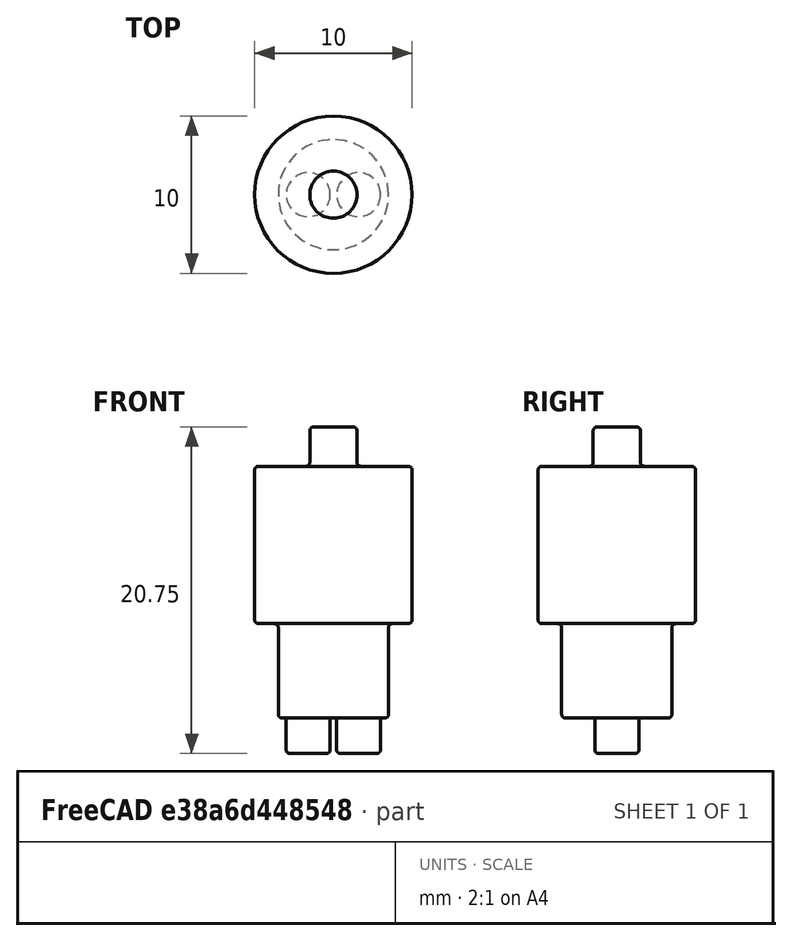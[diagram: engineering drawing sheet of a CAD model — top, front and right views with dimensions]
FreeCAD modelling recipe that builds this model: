
FCSTD DOCUMENT  (FreeCAD 1.0R38641 +468 (Git))
Label: optode
License: All rights reserved
LicenseURL: https://en.wikipedia.org/wiki/All_rights_reserved
objects: Part::Fillet×7, Part::Cylinder×5, Part::MultiFuse×1
note: 13 computed .brp shape members not serialized (recipe doc carries the construction recipe); baked Part::Feature solids carry a one-line shape summary decoded from their .brp

FEATURE [Part::Cylinder] cylinder
  Angle = 360
  AttacherType = Attacher::AttachEngine3D
  FirstAngle = 0
  Height = 10
  Radius = 5
  SecondAngle = 0
FEATURE [Part::Cylinder] cylinder001
  Angle = 360
  AttacherType = Attacher::AttachEngine3D
  FirstAngle = 0
  Height = 2.5
  Placement = pos=(0,0,10) rot=(0,0,1;0rad)
  Radius = 1.5
  SecondAngle = 0
FEATURE [Part::Cylinder] cylinder002
  Angle = 360
  AttacherType = Attacher::AttachEngine3D
  FirstAngle = 0
  Height = 6
  Placement = pos=(0,0,-6) rot=(0,0,1;0rad)
  Radius = 3.5
  SecondAngle = 0
FEATURE [Part::Cylinder] cylinder003
  Angle = 360
  AttacherType = Attacher::AttachEngine3D
  FirstAngle = 0
  Height = 8.25
  Placement = pos=(-1.6,0,-8.25) rot=(0,0,1;0rad)
  Radius = 1.4
  SecondAngle = 0
FEATURE [Part::Cylinder] cylinder004
  Angle = 360
  AttacherType = Attacher::AttachEngine3D
  FirstAngle = 0
  Height = 8.25
  Placement = pos=(1.6,0,-8.25) rot=(0,0,1;0rad)
  Radius = 1.4
  SecondAngle = 0
FEATURE [Part::MultiFuse] Group
  Refine = true
  Shapes = -> [cylinder,cylinder001,cylinder002,cylinder003,cylinder004]
FEATURE [Part::Fillet] Fillet
  Base = -> Group
  EdgeLinks = -> Group [Edge7]
  Edges = 1 edges r=0.25: [Edge7]
FEATURE [Part::Fillet] Fillet001
  Base = -> Fillet
  EdgeLinks = -> Fillet [Edge11,Edge13]
  Edges = 2 edges r=0.25: [Edge11,Edge13]
FEATURE [Part::Fillet] Fillet002
  Base = -> Fillet001
  EdgeLinks = -> Fillet001 [Edge13]
  Edges = 1 edges r=0.25: [Edge13]
FEATURE [Part::Fillet] Fillet003
  Base = -> Fillet002
  EdgeLinks = -> Fillet002 [Edge8]
  Edges = 1 edges r=0.25: [Edge8]
FEATURE [Part::Fillet] Fillet004
  Base = -> Fillet003
  EdgeLinks = -> Fillet003 [Edge8]
  Edges = 1 edges r=0.25: [Edge8]
FEATURE [Part::Fillet] Fillet005
  Base = -> Fillet004
  EdgeLinks = -> Fillet004 [Edge8]
  Edges = 1 edges r=0.25: [Edge8]
FEATURE [Part::Fillet] Fillet006
  Base = -> Fillet005
  EdgeLinks = -> Fillet005 [Edge8]
  Edges = 1 edges r=0.25: [Edge8]
